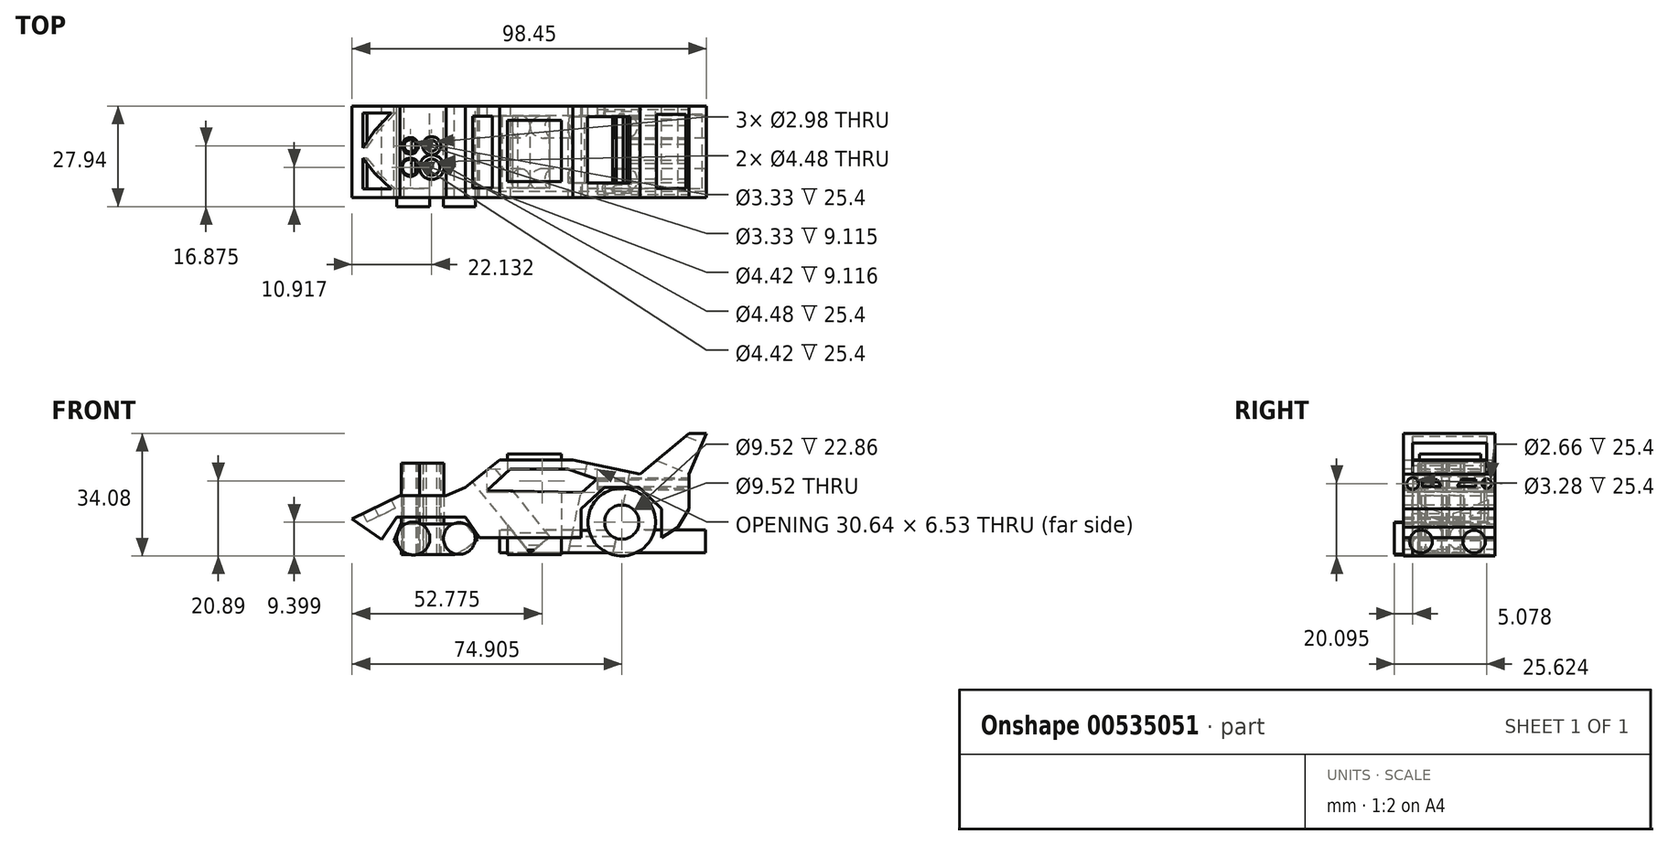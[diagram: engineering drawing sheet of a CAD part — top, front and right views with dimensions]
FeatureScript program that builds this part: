
annotation { "Feature Type Name" : "Feature", "Feature Type Description" : "" }
export const myFeature = defineFeature(function(context is Context, id is Id, definition is map)
    precondition{}
    {
        {
            var Q0;
            Q0=qCreatedBy(makeId("Front.planeOp"),FACE);
            var sketch = newSketch(context, id + "F0", { "sketchPlane" : qUnion([Q0])});
            skCircle(sketch, "E0", {"center": v(33.9, 9.08) * mm, "radius": 9.4 * mm});
            skCircle(sketch, "E1", {"center": v(-11.2, 4.54) * mm, "radius": 4.41 * mm});
            skCircle(sketch, "E2", {"center": v(-23.97, 4.54) * mm, "radius": 4.57 * mm});
            skSolve(sketch);
        }
        {
            var Q0;
            Q0=makeQuery(id+"F0.imprint","IMPRINT",FACE,{"disambiguationData":[TD([[makeQuery(id+"F0.imprint","IMPRINT",EDGE,{"derivedFrom":sQuery(id+"F0.wireOp",EDGE,"E2")}),1.0]])]});
            var Q1;
            Q1=makeQuery(id+"F0.imprint","IMPRINT",FACE,{"disambiguationData":[TD([[makeQuery(id+"F0.imprint","IMPRINT",EDGE,{"derivedFrom":sQuery(id+"F0.wireOp",EDGE,"E1")}),1.0]])]});
            var Q2;
            Q2=makeQuery(id+"F0.imprint","IMPRINT",FACE,{"disambiguationData":[TD([[makeQuery(id+"F0.imprint","IMPRINT",EDGE,{"derivedFrom":sQuery(id+"F0.wireOp",EDGE,"E0")}),1.0]])]});
            extrude(context, id + "F1", {"entities" : qUnion([Q0, Q1, Q2]), "depth" : 22.86 * mm, "offsetDistance" : 25.4 * mm});
        }
        {
            var Q0;
            Q0=qCreatedBy(makeId("Front.planeOp"),FACE);
            var sketch = newSketch(context, id + "F2", { "sketchPlane" : qUnion([Q0])});
            skLineSegment(sketch, "E3", {"start": v(-5.53, 4.82) * mm, "end": v(22.56, 4.82) * mm});
            skLineSegment(sketch, "E4", {"start": v(22.56, 4.82) * mm, "end": v(22.56, 12.77) * mm});
            skLineSegment(sketch, "E5", {"start": v(22.56, 12.77) * mm, "end": v(29.08, 18.73) * mm});
            skLineSegment(sketch, "E6", {"start": v(29.08, 18.73) * mm, "end": v(38.73, 18.73) * mm});
            skLineSegment(sketch, "E7", {"start": v(38.73, 18.73) * mm, "end": v(44.97, 12.77) * mm});
            skLineSegment(sketch, "E8", {"start": v(44.97, 12.77) * mm, "end": v(44.97, 4.82) * mm});
            skLineSegment(sketch, "E9", {"start": v(44.97, 4.82) * mm, "end": v(49.5, 7.66) * mm});
            skLineSegment(sketch, "E10", {"start": v(49.5, 7.66) * mm, "end": v(52.63, 12.77) * mm});
            skLineSegment(sketch, "E11", {"start": v(52.63, 12.77) * mm, "end": v(52.63, 22.41) * mm});
            skLineSegment(sketch, "E12", {"start": v(52.63, 22.41) * mm, "end": v(57.45, 33.76) * mm});
            skLineSegment(sketch, "E13", {"start": v(57.45, 33.76) * mm, "end": v(52.63, 33.76) * mm});
            skLineSegment(sketch, "E14", {"start": v(52.63, 33.76) * mm, "end": v(39.01, 22.41) * mm});
            skLineSegment(sketch, "E15", {"start": v(39.01, 22.41) * mm, "end": v(20.29, 26.39) * mm});
            skLineSegment(sketch, "E16", {"start": v(20.29, 26.39) * mm, "end": v(0, 26.39) * mm});
            skLineSegment(sketch, "E17", {"start": v(0, 26.39) * mm, "end": v(-9.5, 18.73) * mm});
            skLineSegment(sketch, "E18", {"start": v(-9.5, 18.73) * mm, "end": v(-14.9, 16.46) * mm});
            skLineSegment(sketch, "E19", {"start": v(-14.9, 16.46) * mm, "end": v(-27.66, 16.46) * mm});
            skLineSegment(sketch, "E20", {"start": v(-27.66, 16.46) * mm, "end": v(-41, 9.93) * mm});
            skLineSegment(sketch, "E21", {"start": v(-41, 9.93) * mm, "end": v(-32.77, 4.26) * mm});
            skLineSegment(sketch, "E22", {"start": v(-32.77, 4.26) * mm, "end": v(-28.52, 10.42) * mm});
            skLineSegment(sketch, "E23", {"start": v(-28.52, 10.42) * mm, "end": v(-9.5, 10.42) * mm});
            skLineSegment(sketch, "E24", {"start": v(-9.5, 10.42) * mm, "end": v(-5.53, 4.82) * mm});
            skSolve(sketch);
        }
        {
            var Q0;
            Q0=makeQuery(id+"F2.imprint","IMPRINT",FACE,{"disambiguationData":[TD([[makeQuery(id+"F2.imprint","IMPRINT",EDGE,{"derivedFrom":sQuery(id+"F2.wireOp",EDGE,"E3")}),1.0]])]});
            extrude(context, id + "F3", {"entities" : qUnion([Q0]), "depth" : 25.4 * mm, "offsetDistance" : 25.4 * mm});
        }
        {
            var Q0;
            Q0=qCreatedBy(makeId("Right.planeOp"),FACE);
            var sketch = newSketch(context, id + "F4", { "sketchPlane" : qUnion([Q0])});
            skCircle(sketch, "E25", {"center": v(-20.57, 3.69) * mm, "radius": 3.17 * mm});
            skCircle(sketch, "E26", {"center": v(-4.11, 3.69) * mm, "radius": 2.55 * mm});
            skSolve(sketch);
        }
        {
            var Q0;
            Q0=makeQuery(id+"F4.imprint","IMPRINT",FACE,{"disambiguationData":[TD([[makeQuery(id+"F4.imprint","IMPRINT",EDGE,{"derivedFrom":sQuery(id+"F4.wireOp",EDGE,"E25")}),1.0]])]});
            extrude(context, id + "F5", {"entities" : qUnion([Q0]), "depth" : 57.15 * mm, "offsetDistance" : 25.4 * mm});
        }
        {
            var Q0;
            Q0=makeQuery(id+"F1.opExtrude","CAP_FACE",FACE,{"disambiguationData":[OSD([sQuery(id+"F0.wireOp",EDGE,"E0")])],"isStart":false});
            extrude(context, id + "F6", {"entities" : qUnion([Q0]), "depth" : 2.54 * mm, "offsetDistance" : 25.4 * mm});
        }
        {
            var Q0;
            Q0=makeQuery(id+"F1.opExtrude","CAP_FACE",FACE,{"disambiguationData":[OSD([sQuery(id+"F0.wireOp",EDGE,"E1")])],"isStart":false});
            var Q1;
            Q1=makeQuery(id+"F1.opExtrude","CAP_FACE",FACE,{"disambiguationData":[OSD([sQuery(id+"F0.wireOp",EDGE,"E2")])],"isStart":false});
            extrude(context, id + "F7", {"entities" : qUnion([Q0, Q1]), "depth" : 2.54 * mm, "offsetDistance" : 25.4 * mm});
        }
        {
            var Q0;
            Q0=qCreatedBy(makeId("Right.planeOp"),FACE);
            var sketch = newSketch(context, id + "F8", { "sketchPlane" : qUnion([Q0])});
            skCircle(sketch, "E27", {"center": v(-5.82, 3.69) * mm, "radius": 3.12 * mm});
            skSolve(sketch);
        }
        {
            var Q0;
            Q0 = qSketchRegion(id + "F8", true);
            extrude(context, id + "F9", {"entities" : qUnion([Q0]), "depth" : 57.15 * mm, "offsetDistance" : 25.4 * mm});
        }
        {
            var Q0;
            Q0=qCreatedBy(makeId("Front.planeOp"),FACE);
            var sketch = newSketch(context, id + "F10", { "sketchPlane" : qUnion([Q0])});
            skLineSegment(sketch, "E28", {"start": v(-3.55, 17.87) * mm, "end": v(2.98, 23.83) * mm});
            skLineSegment(sketch, "E29", {"start": v(2.98, 23.83) * mm, "end": v(18.87, 23.83) * mm});
            skLineSegment(sketch, "E30", {"start": v(18.87, 23.83) * mm, "end": v(27.1, 21) * mm});
            skLineSegment(sketch, "E31", {"start": v(27.1, 21) * mm, "end": v(22.84, 17.3) * mm});
            skLineSegment(sketch, "E32", {"start": v(22.84, 17.3) * mm, "end": v(-3.55, 17.87) * mm});
            skSolve(sketch);
        }
        {
            var Q0;
            Q0=makeQuery(id+"F10.imprint","IMPRINT",FACE,{"disambiguationData":[TD([[makeQuery(id+"F10.imprint","IMPRINT",EDGE,{"derivedFrom":sQuery(id+"F10.wireOp",EDGE,"E28")}),-1.0]])]});
            extrude(context, id + "F11", {"entities" : qUnion([Q0]), "operationType" : NewBodyOperationType.ADD, "depth" : 27.94 * mm, "offsetDistance" : 25.4 * mm});
        }
        {
            var Q0;
            Q0=qCreatedBy(makeId("Front.planeOp"),FACE);
            var sketch = newSketch(context, id + "F12", { "sketchPlane" : qUnion([Q0])});
            skLineSegment(sketch, "E33", {"start": v(-27.38, 8.51) * mm, "end": v(-9.5, 8.51) * mm});
            skLineSegment(sketch, "E34", {"start": v(-9.5, 8.51) * mm, "end": v(-6.1, 4.26) * mm});
            skLineSegment(sketch, "E35", {"start": v(-6.1, 4.26) * mm, "end": v(-9.5, 1.53) * mm});
            skLineSegment(sketch, "E36", {"start": v(-9.5, 1.53) * mm, "end": v(-12.63, 0) * mm});
            skLineSegment(sketch, "E37", {"start": v(-12.63, 0) * mm, "end": v(-26.53, 0) * mm});
            skLineSegment(sketch, "E38", {"start": v(-26.53, 0) * mm, "end": v(-29.37, 3.97) * mm});
            skLineSegment(sketch, "E39", {"start": v(-29.37, 3.97) * mm, "end": v(-27.38, 8.51) * mm});
            skSolve(sketch);
        }
        {
            var Q0;
            Q0=makeQuery(id+"F7.opExtrude","CAP_FACE",FACE,{"disambiguationData":[OSD([sQuery(id+"F0.wireOp",EDGE,"E2")])],"isStart":false});
            var Q1;
            Q1=makeQuery(id+"F7.opExtrude","CAP_FACE",FACE,{"disambiguationData":[OSD([sQuery(id+"F0.wireOp",EDGE,"E1")])],"isStart":false});
            extrude(context, id + "F13", {"entities" : qUnion([Q0, Q1]), "depth" : 2.54 * mm, "offsetDistance" : 25.4 * mm});
        }
        {
            var Q0;
            Q0=makeQuery(id+"F12.imprint","IMPRINT",FACE,{"disambiguationData":[TD([[makeQuery(id+"F12.imprint","IMPRINT",EDGE,{"derivedFrom":sQuery(id+"F12.wireOp",EDGE,"E33")}),-1.0]])]});
            extrude(context, id + "F14", {"entities" : qUnion([Q0]), "depth" : 25.4 * mm, "offsetDistance" : 25.4 * mm});
        }
        {
            var Q0;
            Q0=qCreatedBy(makeId("Top.planeOp"),FACE);
            var sketch = newSketch(context, id + "F15", { "sketchPlane" : qUnion([Q0])});
            skCircle(sketch, "E40", {"center": v(-24.83, -11.07) * mm, "radius": 2.29 * mm});
            skCircle(sketch, "E41", {"center": v(-18.87, -11.07) * mm, "radius": 2.54 * mm});
            skCircle(sketch, "E42", {"center": v(-18.87, -17.02) * mm, "radius": 3.42 * mm});
            skCircle(sketch, "E43", {"center": v(-24.83, -17.02) * mm, "radius": 2.54 * mm});
            skSolve(sketch);
        }
        {
            var Q0;
            {var subQ0=sQuery(id+"F15.wireOp",EDGE,"E42");var subQ1=makeQuery(id+"F15.imprint","INTERSECT",VERTEX,{"derivedFrom":[sQuery(id+"F15.wireOp",EDGE,"E41"),subQ0]});Q0=makeQuery(id+"F15.imprint","IMPRINT",FACE,{"disambiguationData":[TD([[makeQuery(id+"F15.imprint","IMPRINT",EDGE,{"disambiguationData":[TD([[subQ1,-1.0]])],"derivedFrom":subQ0}),1.0]])]});}
            var Q1;
            Q1=makeQuery(id+"F15.imprint","IMPRINT",FACE,{"disambiguationData":[TD([[makeQuery(id+"F15.imprint","IMPRINT",EDGE,{"derivedFrom":sQuery(id+"F15.wireOp",EDGE,"E43")}),1.0]])]});
            var Q2;
            Q2=makeQuery(id+"F15.imprint","IMPRINT",FACE,{"disambiguationData":[TD([[makeQuery(id+"F15.imprint","IMPRINT",EDGE,{"derivedFrom":sQuery(id+"F15.wireOp",EDGE,"E40")}),1.0]])]});
            var Q3;
            Q3=makeQuery(id+"F15.imprint","IMPRINT",FACE,{"disambiguationData":[TD([[makeQuery(id+"F15.imprint","IMPRINT",EDGE,{"derivedFrom":sQuery(id+"F15.wireOp",EDGE,"E41")}),1.0]])]});
            extrude(context, id + "F16", {"entities" : qUnion([Q0, Q1, Q2, Q3]), "depth" : 25.4 * mm, "offsetDistance" : 25.4 * mm});
        }
        {
            var Q0;
            Q0=qCreatedBy(makeId("Top.planeOp"),FACE);
            var sketch = newSketch(context, id + "F17", { "sketchPlane" : qUnion([Q0])});
            skLineSegment(sketch, "E44", {"start": v(2.13, -3.97) * mm, "end": v(17.17, -3.97) * mm});
            skLineSegment(sketch, "E45", {"start": v(17.17, -3.97) * mm, "end": v(17.17, -21) * mm});
            skLineSegment(sketch, "E46", {"start": v(17.17, -21) * mm, "end": v(2.13, -21) * mm});
            skLineSegment(sketch, "E47", {"start": v(2.13, -21) * mm, "end": v(2.13, -3.97) * mm});
            skSolve(sketch);
        }
        {
            var Q0;
            Q0=makeQuery(id+"F17.imprint","IMPRINT",FACE,{"disambiguationData":[TD([[makeQuery(id+"F17.imprint","IMPRINT",EDGE,{"derivedFrom":sQuery(id+"F17.wireOp",EDGE,"E44")}),-1.0]])]});
            extrude(context, id + "F18", {"entities" : qUnion([Q0]), "depth" : 27.94 * mm, "offsetDistance" : 25.4 * mm});
        }
        {
            var Q0;
            Q0=makeQuery(id+"F11.opExtrude","CAP_FACE",FACE,{"disambiguationData":[OSD([sQuery(id+"F10.wireOp",EDGE,"E28"),sQuery(id+"F10.wireOp",EDGE,"E29"),sQuery(id+"F10.wireOp",EDGE,"E30"),sQuery(id+"F10.wireOp",EDGE,"E31"),sQuery(id+"F10.wireOp",EDGE,"E32")])],"isStart":false});
            extrude(context, id + "F19", {"entities" : qUnion([Q0]), "operationType" : NewBodyOperationType.REMOVE, "oppositeDirection" : true, "depth" : 27.94 * mm, "offsetDistance" : 25.4 * mm});
        }
        {
            var Q0;
            Q0=makeQuery(id+"F6.opExtrude","CAP_FACE",FACE,{"disambiguationData":[OSD([sQuery(id+"F0.wireOp",EDGE,"E0")])],"isStart":false});
            var sketch = newSketch(context, id + "F20", { "sketchPlane" : qUnion([Q0])});
            skCircle(sketch, "E48", {"center": v(33.9, 9.08) * mm, "radius": 4.76 * mm});
            skSolve(sketch);
        }
        {
            var Q0;
            Q0=makeQuery(id+"F20.imprint","IMPRINT",FACE,{"disambiguationData":[TD([[makeQuery(id+"F20.imprint","IMPRINT",EDGE,{"derivedFrom":sQuery(id+"F20.wireOp",EDGE,"E48")}),1.0]])]});
            extrude(context, id + "F21", {"entities" : qUnion([Q0]), "operationType" : NewBodyOperationType.REMOVE, "oppositeDirection" : true, "depth" : 25.4 * mm, "offsetDistance" : 25.4 * mm});
        }
        {
            var Q0;
            Q0=makeQuery(id+"F3.opExtrude","SWEPT_FACE",FACE,{"disambiguationData":[OSD([sQuery(id+"F2.wireOp",EDGE,"E12")])]});
            var sketch = newSketch(context, id + "F22", { "sketchPlane" : qUnion([Q0])});
            skLineSegment(sketch, "E49", {"start": v(-22.86, 41.21) * mm, "end": v(-22.86, 50.59) * mm});
            skLineSegment(sketch, "E50", {"start": v(-22.86, 50.59) * mm, "end": v(-2.32, 50.59) * mm});
            skLineSegment(sketch, "E51", {"start": v(-2.32, 50.59) * mm, "end": v(-2.32, 41.21) * mm});
            skLineSegment(sketch, "E52", {"start": v(-2.32, 41.21) * mm, "end": v(-22.86, 41.21) * mm});
            skSolve(sketch);
        }
        {
            var Q0;
            Q0=makeQuery(id+"F22.imprint","IMPRINT",FACE,{"disambiguationData":[TD([[makeQuery(id+"F22.imprint","IMPRINT",EDGE,{"derivedFrom":sQuery(id+"F22.wireOp",EDGE,"E49")}),-1.0]])]});
            extrude(context, id + "F23", {"entities" : qUnion([Q0]), "operationType" : NewBodyOperationType.REMOVE, "oppositeDirection" : true, "depth" : 25.4 * mm, "offsetDistance" : 25.4 * mm});
        }
        {
            var Q0;
            Q0=makeQuery(id+"F16.opExtrude","CAP_FACE",FACE,{"disambiguationData":[OSD([sQuery(id+"F15.wireOp",EDGE,"E42")])],"isStart":false});
            var sketch = newSketch(context, id + "F24", { "sketchPlane" : qUnion([Q0])});
            skCircle(sketch, "E53", {"center": v(-18.87, -17.02) * mm, "radius": 2.24 * mm});
            skSolve(sketch);
        }
        {
            var Q0;
            Q0=makeQuery(id+"F24.imprint","IMPRINT",FACE,{"disambiguationData":[TD([[makeQuery(id+"F24.imprint","IMPRINT",EDGE,{"derivedFrom":sQuery(id+"F24.wireOp",EDGE,"E53")}),1.0]])]});
            extrude(context, id + "F25", {"entities" : qUnion([Q0]), "operationType" : NewBodyOperationType.REMOVE, "oppositeDirection" : true, "depth" : 25.4 * mm, "offsetDistance" : 25.4 * mm});
        }
        {
            var Q0;
            Q0=makeQuery(id+"F16.opExtrude","CAP_FACE",FACE,{"disambiguationData":[OSD([sQuery(id+"F15.wireOp",EDGE,"E41")])],"isStart":false});
            var sketch = newSketch(context, id + "F26", { "sketchPlane" : qUnion([Q0])});
            skCircle(sketch, "E54", {"center": v(-18.87, -11.07) * mm, "radius": 1.5 * mm});
            skSolve(sketch);
        }
        {
            var Q0;
            Q0=makeQuery(id+"F26.imprint","IMPRINT",FACE,{"disambiguationData":[TD([[makeQuery(id+"F26.imprint","IMPRINT",EDGE,{"derivedFrom":sQuery(id+"F26.wireOp",EDGE,"E54")}),1.0]])]});
            extrude(context, id + "F27", {"entities" : qUnion([Q0]), "operationType" : NewBodyOperationType.REMOVE, "oppositeDirection" : true, "depth" : 25.4 * mm, "offsetDistance" : 25.4 * mm});
        }
        {
            var Q0;
            Q0=makeQuery(id+"F16.opExtrude","CAP_FACE",FACE,{"disambiguationData":[OSD([sQuery(id+"F15.wireOp",EDGE,"E40")])],"isStart":false});
            var sketch = newSketch(context, id + "F28", { "sketchPlane" : qUnion([Q0])});
            skCircle(sketch, "E55", {"center": v(-24.83, -11.07) * mm, "radius": 1.67 * mm});
            skSolve(sketch);
        }
        {
            var Q0;
            Q0=makeQuery(id+"F28.imprint","IMPRINT",FACE,{"disambiguationData":[TD([[makeQuery(id+"F28.imprint","IMPRINT",EDGE,{"derivedFrom":sQuery(id+"F28.wireOp",EDGE,"E55")}),1.0]])]});
            extrude(context, id + "F29", {"entities" : qUnion([Q0]), "operationType" : NewBodyOperationType.REMOVE, "oppositeDirection" : true, "depth" : 25.4 * mm, "offsetDistance" : 25.4 * mm});
        }
        {
            var Q0;
            Q0=makeQuery(id+"F16.opExtrude","CAP_FACE",FACE,{"disambiguationData":[OSD([sQuery(id+"F15.wireOp",EDGE,"E43")])],"isStart":false});
            var sketch = newSketch(context, id + "F30", { "sketchPlane" : qUnion([Q0])});
            skCircle(sketch, "E56", {"center": v(-24.83, -17.02) * mm, "radius": 2.2 * mm});
            skSolve(sketch);
        }
        {
            var Q0;
            Q0=makeQuery(id+"F30.imprint","IMPRINT",FACE,{"disambiguationData":[TD([[makeQuery(id+"F30.imprint","IMPRINT",EDGE,{"derivedFrom":sQuery(id+"F30.wireOp",EDGE,"E56")}),1.0]])]});
            extrude(context, id + "F31", {"entities" : qUnion([Q0]), "operationType" : NewBodyOperationType.REMOVE, "oppositeDirection" : true, "depth" : 25.4 * mm, "offsetDistance" : 25.4 * mm});
        }
        {
            var Q0;
            Q0=makeQuery(id+"F3.opExtrude","SWEPT_FACE",FACE,{"disambiguationData":[OSD([sQuery(id+"F2.wireOp",EDGE,"E11")])]});
            var sketch = newSketch(context, id + "F32", { "sketchPlane" : qUnion([Q0])});
            skCircle(sketch, "E57", {"center": v(-22.86, 19.78) * mm, "radius": 1.64 * mm});
            skCircle(sketch, "E58", {"center": v(-2.32, 19.78) * mm, "radius": 1.33 * mm});
            skSolve(sketch);
        }
        {
            var Q0;
            Q0=makeQuery(id+"F32.imprint","IMPRINT",FACE,{"disambiguationData":[TD([[makeQuery(id+"F32.imprint","IMPRINT",EDGE,{"derivedFrom":sQuery(id+"F32.wireOp",EDGE,"E57")}),-1.0]])]});
            var sketch = newSketch(context, id + "F33", { "sketchPlane" : qUnion([Q0])});
            skLineSegment(sketch, "E59", {"start": v(-20.2, 20.98) * mm, "end": v(-20.2, 18.93) * mm});
            skLineSegment(sketch, "E60", {"start": v(-20.2, 18.93) * mm, "end": v(-15.02, 18.93) * mm});
            skLineSegment(sketch, "E61", {"start": v(-15.02, 18.93) * mm, "end": v(-15.99, 20.86) * mm});
            skLineSegment(sketch, "E62", {"start": v(-15.99, 20.86) * mm, "end": v(-20.2, 20.98) * mm});
            skLineSegment(sketch, "E63", {"start": v(-5.38, 20.98) * mm, "end": v(-5.38, 18.93) * mm});
            skLineSegment(sketch, "E64", {"start": v(-5.38, 18.93) * mm, "end": v(-10.56, 18.93) * mm});
            skLineSegment(sketch, "E65", {"start": v(-10.56, 18.93) * mm, "end": v(-9.24, 20.98) * mm});
            skLineSegment(sketch, "E66", {"start": v(-9.24, 20.98) * mm, "end": v(-5.38, 20.98) * mm});
            skSolve(sketch);
        }
        {
            var Q0;
            Q0=makeQuery(id+"F32.imprint","IMPRINT",FACE,{"disambiguationData":[TD([[makeQuery(id+"F32.imprint","IMPRINT",EDGE,{"derivedFrom":sQuery(id+"F32.wireOp",EDGE,"E57")}),1.0]])]});
            var Q1;
            Q1=makeQuery(id+"F33.imprint","IMPRINT",FACE,{"disambiguationData":[TD([[makeQuery(id+"F33.imprint","IMPRINT",EDGE,{"derivedFrom":sQuery(id+"F33.wireOp",EDGE,"E59")}),1.0]])]});
            var Q2;
            Q2=makeQuery(id+"F33.imprint","IMPRINT",FACE,{"disambiguationData":[TD([[makeQuery(id+"F33.imprint","IMPRINT",EDGE,{"derivedFrom":sQuery(id+"F33.wireOp",EDGE,"E63")}),-1.0]])]});
            var Q3;
            Q3=makeQuery(id+"F32.imprint","IMPRINT",FACE,{"disambiguationData":[TD([[makeQuery(id+"F32.imprint","IMPRINT",EDGE,{"derivedFrom":sQuery(id+"F32.wireOp",EDGE,"E58")}),1.0]])]});
            extrude(context, id + "F34", {"entities" : qUnion([Q0, Q1, Q2, Q3]), "operationType" : NewBodyOperationType.REMOVE, "oppositeDirection" : true, "depth" : 25.4 * mm, "offsetDistance" : 25.4 * mm});
        }
        {
            var Q0;
            Q0=makeQuery(id+"F3.opExtrude","SWEPT_FACE",FACE,{"disambiguationData":[OSD([sQuery(id+"F2.wireOp",EDGE,"E17")])]});
            var sketch = newSketch(context, id + "F35", { "sketchPlane" : qUnion([Q0])});
            skLineSegment(sketch, "E67", {"start": v(14.02, -2.9) * mm, "end": v(6.89, -2.9) * mm});
            skLineSegment(sketch, "E68", {"start": v(6.89, -2.9) * mm, "end": v(6.89, -22.76) * mm});
            skLineSegment(sketch, "E69", {"start": v(6.89, -22.76) * mm, "end": v(14.02, -22.76) * mm});
            skLineSegment(sketch, "E70", {"start": v(14.02, -22.76) * mm, "end": v(14.02, -2.9) * mm});
            skSolve(sketch);
        }
        {
            var Q0;
            Q0=makeQuery(id+"F35.imprint","IMPRINT",FACE,{"disambiguationData":[TD([[makeQuery(id+"F35.imprint","IMPRINT",EDGE,{"derivedFrom":sQuery(id+"F35.wireOp",EDGE,"E67")}),1.0]])]});
            extrude(context, id + "F36", {"entities" : qUnion([Q0]), "operationType" : NewBodyOperationType.REMOVE, "oppositeDirection" : true, "depth" : 25.4 * mm, "offsetDistance" : 25.4 * mm});
        }
        {
            var Q0;
            Q0=makeQuery(id+"F3.opExtrude","SWEPT_FACE",FACE,{"disambiguationData":[OSD([sQuery(id+"F2.wireOp",EDGE,"E15")])]});
            var sketch = newSketch(context, id + "F37", { "sketchPlane" : qUnion([Q0])});
            skLineSegment(sketch, "E71", {"start": v(18.5, -21.42) * mm, "end": v(30.68, -21.42) * mm});
            skLineSegment(sketch, "E72", {"start": v(30.68, -21.42) * mm, "end": v(30.68, -2.98) * mm});
            skLineSegment(sketch, "E73", {"start": v(30.68, -2.98) * mm, "end": v(18.5, -2.98) * mm});
            skLineSegment(sketch, "E74", {"start": v(18.5, -2.98) * mm, "end": v(18.5, -21.42) * mm});
            skSolve(sketch);
        }
        {
            var Q0;
            Q0=makeQuery(id+"F37.imprint","IMPRINT",FACE,{"disambiguationData":[TD([[makeQuery(id+"F37.imprint","IMPRINT",EDGE,{"derivedFrom":sQuery(id+"F37.wireOp",EDGE,"E71")}),1.0]])]});
            extrude(context, id + "F38", {"entities" : qUnion([Q0]), "operationType" : NewBodyOperationType.REMOVE, "oppositeDirection" : true, "depth" : 25.4 * mm, "offsetDistance" : 25.4 * mm});
        }
        {
            var Q0;
            Q0=makeQuery(id+"F3.opExtrude","SWEPT_FACE",FACE,{"disambiguationData":[OSD([sQuery(id+"F2.wireOp",EDGE,"E20")])]});
            var sketch = newSketch(context, id + "F39", { "sketchPlane" : qUnion([Q0])});
            skLineSegment(sketch, "E75", {"start": v(-20.33, -1.99) * mm, "end": v(-29.03, -1.99) * mm});
            skLineSegment(sketch, "E76", {"start": v(-29.03, -1.99) * mm, "end": v(-29.03, -11.63) * mm});
            skLineSegment(sketch, "E77", {"start": v(-29.03, -11.63) * mm, "end": v(-25.43, -6.8) * mm});
            skPoint(sketch, "E77.endSnap0", {"position": v(-29.03, -6.8) * mm});
            skLineSegment(sketch, "E78", {"start": v(-20.33, -1.99) * mm, "end": v(-25.43, -6.8) * mm});
            skLineSegment(sketch, "E79", {"start": v(-20.33, -22.98) * mm, "end": v(-29.03, -22.98) * mm});
            skLineSegment(sketch, "E80", {"start": v(-29.03, -22.98) * mm, "end": v(-29.03, -14.47) * mm});
            skLineSegment(sketch, "E81", {"start": v(-29.03, -14.47) * mm, "end": v(-25.43, -18.73) * mm});
            skPoint(sketch, "E81.endSnap0", {"position": v(-29.03, -18.73) * mm});
            skLineSegment(sketch, "E82", {"start": v(-25.43, -18.73) * mm, "end": v(-20.33, -22.98) * mm});
            skSolve(sketch);
        }
        {
            var Q0;
            Q0=makeQuery(id+"F39.imprint","IMPRINT",FACE,{"disambiguationData":[TD([[makeQuery(id+"F39.imprint","IMPRINT",EDGE,{"derivedFrom":sQuery(id+"F39.wireOp",EDGE,"E75")}),1.0]])]});
            var Q1;
            Q1=makeQuery(id+"F39.imprint","IMPRINT",FACE,{"disambiguationData":[TD([[makeQuery(id+"F39.imprint","IMPRINT",EDGE,{"derivedFrom":sQuery(id+"F39.wireOp",EDGE,"E79")}),-1.0]])]});
            extrude(context, id + "F40", {"entities" : qUnion([Q0, Q1]), "operationType" : NewBodyOperationType.REMOVE, "oppositeDirection" : true, "depth" : 2.54 * mm, "offsetDistance" : 25.4 * mm});
        }
    });
